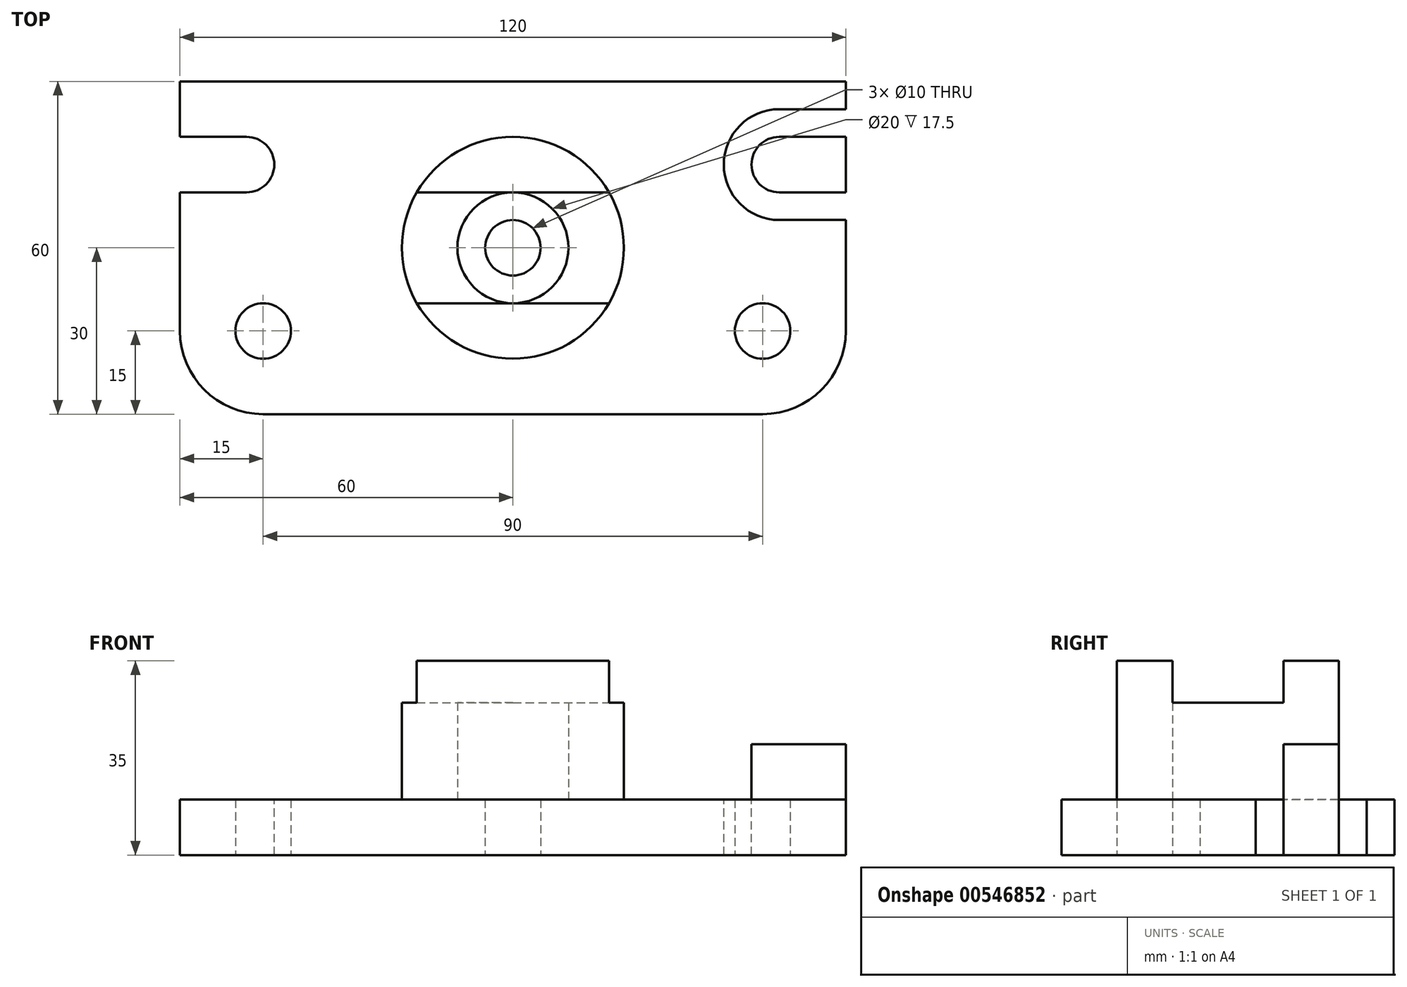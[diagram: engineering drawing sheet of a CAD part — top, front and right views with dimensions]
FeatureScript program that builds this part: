
annotation { "Feature Type Name" : "Feature", "Feature Type Description" : "" }
export const myFeature = defineFeature(function(context is Context, id is Id, definition is map)
    precondition{}
    {
        {
            var Q0;
            Q0=qCreatedBy(makeId("Top.planeOp"),FACE);
            var sketch = newSketch(context, id + "F0", { "sketchPlane" : qUnion([Q0])});
            skLineSegment(sketch, "E0", {"start": v(-60, 30) * mm, "end": v(60, 30) * mm});
            skLineSegment(sketch, "E1", {"start": v(60, 30) * mm, "end": v(60, -15) * mm});
            skLineSegment(sketch, "E2", {"start": v(45, -30) * mm, "end": v(-45, -30) * mm});
            skLineSegment(sketch, "E3", {"start": v(-60, -15) * mm, "end": v(-60, 30) * mm});
            skPoint(sketch, "E4.visualSharp", {"position": v(60, -30) * mm});
            skArc(sketch, "E4.filletArc", {"start": v(45, -30) * mm, "mid": v(55.6, -25.6) * mm, "end": v(60, -15) * mm});
            skPoint(sketch, "E5.visualSharp", {"position": v(-60, -30) * mm});
            skArc(sketch, "E5.filletArc", {"start": v(-60, -15) * mm, "mid": v(-55.6, -25.6) * mm, "end": v(-45, -30) * mm});
            skSolve(sketch);
        }
        {
            var Q0;
            Q0=makeQuery(id+"F0.imprint","IMPRINT",FACE,{"disambiguationData":[TD([[makeQuery(id+"F0.imprint","IMPRINT",EDGE,{"derivedFrom":sQuery(id+"F0.wireOp",EDGE,"E0")}),-1.0]])]});
            var Q1;
            Q1=makeQuery(id+"F0.imprint","IMPRINT",FACE,{"disambiguationData":[TD([[makeQuery(id+"F0.imprint","IMPRINT",EDGE,{"derivedFrom":sQuery(id+"F0.wireOp",EDGE,"jAcdVFmT-cDeR-TPM5-7F6G-FVIwFFzWRn1m")}),1.0]])]});
            extrude(context, id + "F1", {"entities" : qUnion([Q0, Q1]), "depth" : 20 * mm, "offsetDistance" : 25 * mm});
        }
        {
            var Q0;
            Q0=makeQuery(id+"F1.opExtrude","CAP_FACE",FACE,{"disambiguationData":[OSD([sQuery(id+"F0.wireOp",EDGE,"E0"),sQuery(id+"F0.wireOp",EDGE,"E1"),sQuery(id+"F0.wireOp",EDGE,"E2"),sQuery(id+"F0.wireOp",EDGE,"E3"),sQuery(id+"F0.wireOp",EDGE,"E4.filletArc"),sQuery(id+"F0.wireOp",EDGE,"E5.filletArc")])],"isStart":false});
            var sketch = newSketch(context, id + "F2", { "sketchPlane" : qUnion([Q0])});
            skCircle(sketch, "E6", {"center": v(0, 0) * mm, "radius": 20 * mm});
            skSolve(sketch);
        }
        {
            var Q0;
            Q0=makeQuery(id+"F2.imprint","IMPRINT",FACE,{"disambiguationData":[TD([[makeQuery(id+"F2.imprint","IMPRINT",EDGE,{"derivedFrom":sQuery(id+"F2.wireOp",EDGE,"E6")}),1.0]])]});
            extrude(context, id + "F3", {"entities" : qUnion([Q0]), "operationType" : NewBodyOperationType.ADD, "depth" : 15 * mm, "offsetDistance" : 25 * mm});
        }
        {
            var Q0;
            Q0=makeQuery(id+"F1.opExtrude","CAP_FACE",FACE,{"disambiguationData":[OSD([sQuery(id+"F0.wireOp",EDGE,"E0"),sQuery(id+"F0.wireOp",EDGE,"E1"),sQuery(id+"F0.wireOp",EDGE,"E2"),sQuery(id+"F0.wireOp",EDGE,"E3"),sQuery(id+"F0.wireOp",EDGE,"E4.filletArc"),sQuery(id+"F0.wireOp",EDGE,"E5.filletArc")])],"isStart":false});
            var sketch = newSketch(context, id + "F4", { "sketchPlane" : qUnion([Q0])});
            skPoint(sketch, "E7", {"position": v(45, -15) * mm});
            skPoint(sketch, "E8", {"position": v(-45, -15) * mm});
            skPoint(sketch, "E9", {"position": v(0, 0) * mm});
            skSolve(sketch);
        }
        {
            var Q0;
            Q0=makeQuery(id+"F4.imprint","IMPRINT",FACE,{"disambiguationData":[TD([[makeQuery(id+"F4.imprint","IMPRINT",EDGE,{"derivedFrom":makeQuery(id+"F1.opExtrude","CAP_EDGE",EDGE,{"disambiguationData":[OSD([sQuery(id+"F0.wireOp",EDGE,"E0")])],"isStart":false})}),-1.0]])]});
            var sketch = newSketch(context, id + "F5", { "sketchPlane" : qUnion([Q0])});
            skArc(sketch, "E10", {"start": v(-48, 5) * mm, "mid": v(-38, 15) * mm, "end": v(-48, 25) * mm});
            skArc(sketch, "E11", {"start": v(-48, 10) * mm, "mid": v(-43, 15) * mm, "end": v(-48, 20) * mm});
            skLineSegment(sketch, "E12", {"start": v(-48, 20) * mm, "end": v(-65.53, 20) * mm});
            skLineSegment(sketch, "E13", {"start": v(-48, 10) * mm, "end": v(-65.53, 10) * mm});
            skLineSegment(sketch, "E14", {"start": v(-65.53, 20) * mm, "end": v(-65.53, 10) * mm});
            skLineSegment(sketch, "E15", {"start": v(0, 47.07) * mm, "end": v(0, -50.47) * mm, "construction": true});
            skArc(sketch, "E16.MirrorCS", {"start": v(48, 5) * mm, "mid": v(38, 15) * mm, "end": v(48, 25) * mm});
            skArc(sketch, "E17.MirrorCS", {"start": v(48, 10) * mm, "mid": v(43, 15) * mm, "end": v(48, 20) * mm});
            skLineSegment(sketch, "E18.MirrorCS", {"start": v(48, 20) * mm, "end": v(65.53, 20) * mm});
            skLineSegment(sketch, "E19.MirrorCS", {"start": v(48, 10) * mm, "end": v(65.53, 10) * mm});
            skLineSegment(sketch, "E20.MirrorCS", {"start": v(65.53, 20) * mm, "end": v(65.53, 10) * mm});
            skPoint(sketch, "E21.MirrorCS.end.orphan", {"position": v(56.28, 25) * mm});
            skPoint(sketch, "E21.MirrorCS.start.orphan", {"position": v(48, 25) * mm});
            skPoint(sketch, "E22.MirrorCS.end.orphan", {"position": v(56.22, 5) * mm});
            skPoint(sketch, "E22.MirrorCS.start.orphan", {"position": v(48, 5) * mm});
            skPoint(sketch, "E23.end.orphan", {"position": v(-56.28, 25) * mm});
            skPoint(sketch, "E24.end.orphan", {"position": v(-56.22, 5) * mm});
            skLineSegment(sketch, "E25", {"start": v(48, 25) * mm, "end": v(71.02, 25) * mm});
            skLineSegment(sketch, "E26", {"start": v(-48, 25) * mm, "end": v(-72.01, 25) * mm});
            skLineSegment(sketch, "E27", {"start": v(-48, 5) * mm, "end": v(-72.35, 5) * mm});
            skLineSegment(sketch, "E28", {"start": v(-72.01, 25) * mm, "end": v(-72.35, 5) * mm});
            skLineSegment(sketch, "E29.MirrorCS", {"start": v(0, -37.07) * mm, "end": v(0, 60.47) * mm, "construction": true});
            skLineSegment(sketch, "E30", {"start": v(48, 5) * mm, "end": v(71.69, 5) * mm});
            skLineSegment(sketch, "E31", {"start": v(71.69, 5) * mm, "end": v(71.02, 25) * mm});
            skSolve(sketch);
        }
        {
            var Q0;
            {var subQ0=sQuery(id+"F5.wireOp",EDGE,"E11");Q0=makeQuery(id+"F5.imprint","IMPRINT",FACE,{"disambiguationData":[TD([[makeQuery(id+"F5.imprint","IMPRINT",EDGE,{"derivedFrom":subQ0}),1.0]])]});}
            var Q1;
            {var subQ0=sQuery(id+"F5.wireOp",EDGE,"E17.MirrorCS");Q1=makeQuery(id+"F5.imprint","IMPRINT",FACE,{"disambiguationData":[TD([[makeQuery(id+"F5.imprint","IMPRINT",EDGE,{"derivedFrom":subQ0}),-1.0]])]});}
            extrude(context, id + "F6", {"entities" : qUnion([Q0, Q1]), "operationType" : NewBodyOperationType.REMOVE, "endBound" : BoundingType.THROUGH_ALL, "oppositeDirection" : true, "depth" : 25 * mm, "offsetDistance" : 25 * mm});
        }
        {
            var Q0;
            {var subQ8=sQuery(id+"F5.wireOp",EDGE,"E10");Q0=makeQuery(id+"F5.imprint","IMPRINT",FACE,{"disambiguationData":[TD([[makeQuery(id+"F5.imprint","IMPRINT",EDGE,{"derivedFrom":subQ8}),1.0]])]});}
            var Q1;
            {var subQ8=sQuery(id+"F5.wireOp",EDGE,"E16.MirrorCS");Q1=makeQuery(id+"F5.imprint","IMPRINT",FACE,{"disambiguationData":[TD([[makeQuery(id+"F5.imprint","IMPRINT",EDGE,{"derivedFrom":subQ8}),-1.0]])]});}
            extrude(context, id + "F7", {"entities" : qUnion([Q0, Q1]), "operationType" : NewBodyOperationType.REMOVE, "oppositeDirection" : true, "depth" : 10 * mm, "offsetDistance" : 25 * mm});
        }
        {
            var Q0;
            Q0=sQuery(id+"F4.wireOp",VERTEX,"E8");
            var Q1;
            Q1=sQuery(id+"F4.wireOp",VERTEX,"E7");
            var Q2;
            Q2=makeQuery(id+"F1.opExtrude","SWEPT_BODY",BODY,{"disambiguationData":[OSD([sQuery(id+"F0.wireOp",EDGE,"E0"),sQuery(id+"F0.wireOp",EDGE,"E1"),sQuery(id+"F0.wireOp",EDGE,"E2"),sQuery(id+"F0.wireOp",EDGE,"E3"),sQuery(id+"F0.wireOp",EDGE,"E4.filletArc"),sQuery(id+"F0.wireOp",EDGE,"E5.filletArc")])]});
            hole(context, id + "F8", {"style" : HoleStyle.C_BORE, "endStyle" : HoleEndStyle.THROUGH, "holeDiameter" : 10 * mm, "cBoreDiameter" : 16 * mm, "cBoreDepth" : 6 * mm, "isTappedThrough" : true, "tappedDepth" : 12 * mm, "tapClearance" : 3, "startFromSketch" : true, "locations" : qUnion([Q0, Q1]), "scope" : qUnion([Q2])});
        }
        {
            var Q0;
            Q0=makeQuery(id+"F3.opExtrude","CAP_FACE",FACE,{"disambiguationData":[OSD([sQuery(id+"F2.wireOp",EDGE,"E6")])],"isStart":false});
            var sketch = newSketch(context, id + "F9", { "sketchPlane" : qUnion([Q0])});
            skPoint(sketch, "E32", {"position": v(0, 0) * mm});
            skSolve(sketch);
        }
        {
            var Q0;
            Q0=sQuery(id+"F9.wireOp",VERTEX,"E32");
            var Q1;
            Q1=makeQuery(id+"F1.opExtrude","SWEPT_BODY",BODY,{"disambiguationData":[OSD([sQuery(id+"F0.wireOp",EDGE,"E0"),sQuery(id+"F0.wireOp",EDGE,"E1"),sQuery(id+"F0.wireOp",EDGE,"E2"),sQuery(id+"F0.wireOp",EDGE,"E3"),sQuery(id+"F0.wireOp",EDGE,"E4.filletArc"),sQuery(id+"F0.wireOp",EDGE,"E5.filletArc")])]});
            hole(context, id + "F10", {"style" : HoleStyle.C_BORE, "endStyle" : HoleEndStyle.THROUGH, "holeDiameter" : 10 * mm, "cBoreDiameter" : 20 * mm, "cBoreDepth" : 25 * mm, "isTappedThrough" : true, "tappedDepth" : 12 * mm, "tapClearance" : 3, "startFromSketch" : true, "locations" : qUnion([Q0]), "scope" : qUnion([Q1])});
        }
        {
            var Q0;
            Q0=makeQuery(id+"F3.opExtrude","CAP_FACE",FACE,{"disambiguationData":[OSD([sQuery(id+"F2.wireOp",EDGE,"E6")])],"isStart":false});
            var sketch = newSketch(context, id + "F11", { "sketchPlane" : qUnion([Q0])});
            skLineSegment(sketch, "E33.bottom", {"start": v(-20, 10) * mm, "end": v(20, 10) * mm});
            skLineSegment(sketch, "E33.top", {"start": v(-20, -10) * mm, "end": v(20, -10) * mm});
            skLineSegment(sketch, "E33.left", {"start": v(-20, 10) * mm, "end": v(-20, -10) * mm});
            skLineSegment(sketch, "E33.right", {"start": v(20, 10) * mm, "end": v(20, -10) * mm});
            skPoint(sketch, "E33.middle", {"position": v(0, 0) * mm});
            skSolve(sketch);
        }
        {
            var Q0;
            {var subQ0=sQuery(id+"F11.wireOp",EDGE,"E33.bottom");var subQ1=makeQuery(id+"F3.opExtrude","CAP_EDGE",EDGE,{"disambiguationData":[OSD([sQuery(id+"F2.wireOp",EDGE,"E6")])],"isStart":false});var subQ2=makeQuery(id+"F11.imprint","INTERSECT",VERTEX,{"disambiguationData":[OD(0.0)],"derivedFrom":[subQ1,subQ0]});Q0=makeQuery(id+"F11.imprint","IMPRINT",FACE,{"disambiguationData":[TD([[makeQuery(id+"F11.imprint","IMPRINT",EDGE,{"disambiguationData":[TD([[subQ2,-1.0]])],"derivedFrom":subQ1}),1.0]])]});}
            var Q1;
            {var subQ0=sQuery(id+"F11.wireOp",EDGE,"E33.bottom");var subQ1=makeQuery(id+"F3.opExtrude","CAP_EDGE",EDGE,{"disambiguationData":[OSD([sQuery(id+"F2.wireOp",EDGE,"E6")])],"isStart":false});var subQ2=makeQuery(id+"F11.imprint","INTERSECT",VERTEX,{"disambiguationData":[OD(1.0)],"derivedFrom":[subQ1,subQ0]});Q1=makeQuery(id+"F11.imprint","IMPRINT",FACE,{"disambiguationData":[TD([[makeQuery(id+"F11.imprint","IMPRINT",EDGE,{"disambiguationData":[TD([[subQ2,1.0]])],"derivedFrom":subQ1}),1.0]])]});}
            extrude(context, id + "F12", {"entities" : qUnion([Q0, Q1]), "operationType" : NewBodyOperationType.REMOVE, "oppositeDirection" : true, "depth" : 7.5 * mm, "offsetDistance" : 25 * mm});
        }
    });
